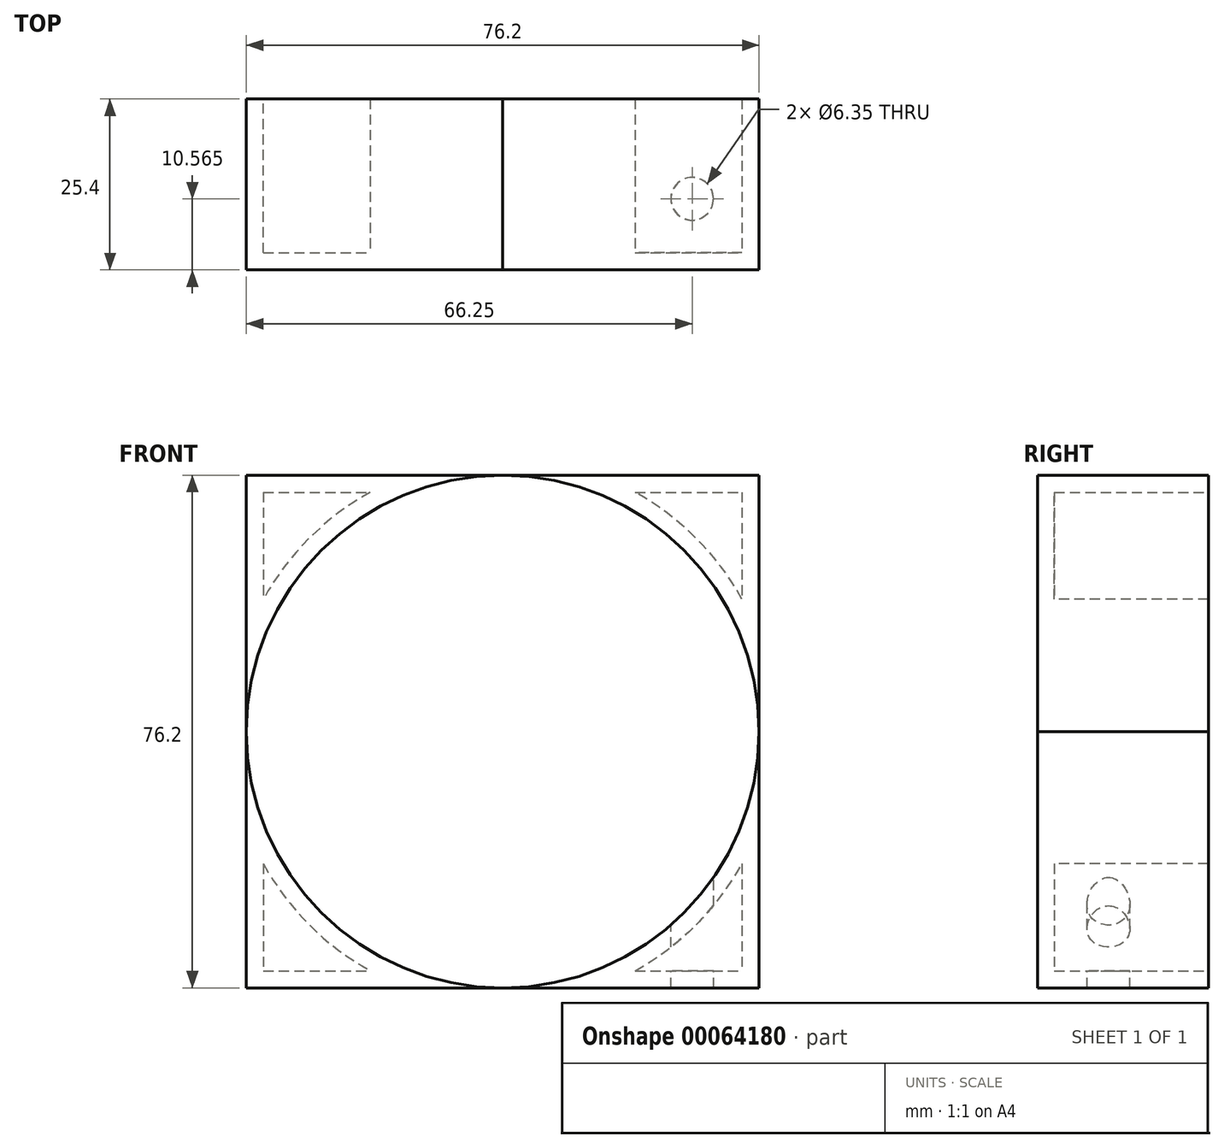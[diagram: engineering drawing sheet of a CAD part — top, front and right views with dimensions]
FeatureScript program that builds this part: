
annotation { "Feature Type Name" : "Feature", "Feature Type Description" : "" }
export const myFeature = defineFeature(function(context is Context, id is Id, definition is map)
    precondition{}
    {
        {
            var Q0;
            Q0=qCreatedBy(makeId("Front.planeOp"),FACE);
            var sketch = newSketch(context, id + "F0", { "sketchPlane" : qUnion([Q0])});
            skLineSegment(sketch, "E0.bottom", {"start": v(-38.1, 38.1) * mm, "end": v(38.1, 38.1) * mm});
            skLineSegment(sketch, "E0.top", {"start": v(-38.1, -38.1) * mm, "end": v(38.1, -38.1) * mm});
            skLineSegment(sketch, "E0.left", {"start": v(-38.1, 38.1) * mm, "end": v(-38.1, -38.1) * mm});
            skLineSegment(sketch, "E0.right", {"start": v(38.1, 38.1) * mm, "end": v(38.1, -38.1) * mm});
            skSolve(sketch);
        }
        {
            var Q0;
            Q0 = qSketchRegion(id + "F0", true);
            extrude(context, id + "F1", {"entities" : qUnion([Q0]), "depth" : 25.4 * mm});
        }
        {
            var Q0;
            Q0=makeQuery(id+"F1.opExtrude","CAP_FACE",FACE,{"disambiguationData":[OSD([sQuery(id+"F0.wireOp",EDGE,"E0.bottom"),sQuery(id+"F0.wireOp",EDGE,"E0.top"),sQuery(id+"F0.wireOp",EDGE,"E0.left"),sQuery(id+"F0.wireOp",EDGE,"E0.right")])],"isStart":false});
            var sketch = newSketch(context, id + "F2", { "sketchPlane" : qUnion([Q0])});
            skCircle(sketch, "E1", {"center": v(0, 0) * mm, "radius": 38.1 * mm});
            skSolve(sketch);
        }
        {
            var Q0;
            {var subQ0=sQuery(id+"F2.wireOp",EDGE,"E1");var subQ1=makeQuery(id+"F2.imprint","INTERSECT",VERTEX,{"derivedFrom":[makeQuery(id+"F1.opExtrude","CAP_EDGE",EDGE,{"disambiguationData":[OSD([sQuery(id+"F0.wireOp",EDGE,"E0.bottom")])],"isStart":false}),subQ0]});Q0=makeQuery(id+"F2.imprint","IMPRINT",FACE,{"disambiguationData":[TD([[makeQuery(id+"F2.imprint","IMPRINT",EDGE,{"disambiguationData":[TD([[subQ1,1.0]])],"derivedFrom":subQ0}),1.0]])]});}
            extrude(context, id + "F3", {"entities" : qUnion([Q0]), "operationType" : NewBodyOperationType.REMOVE, "oppositeDirection" : true, "depth" : 25.4 * mm});
        }
        {
            var Q0;
            {var subQ0=sQuery(id+"F0.wireOp",EDGE,"E0.bottom");var subQ1=sQuery(id+"F0.wireOp",EDGE,"E0.right");Q0=makeQuery(id+"F3.boolean.opBoolean","SPLIT",FACE,{"disambiguationData":[TD([makeQuery(id+"F1.opExtrude","SWEPT_FACE",FACE,{"disambiguationData":[OSD([subQ0])]}),makeQuery(id+"F1.opExtrude","SWEPT_FACE",FACE,{"disambiguationData":[OSD([subQ1])]}),makeQuery(id+"F3.opExtrude","SWEPT_FACE",FACE,{"disambiguationData":[OSD([sQuery(id+"F2.wireOp",EDGE,"E1")])]})])],"derivedFrom":makeQuery(id+"F1.opExtrude","CAP_FACE",FACE,{"disambiguationData":[OSD([subQ0,sQuery(id+"F0.wireOp",EDGE,"E0.top"),sQuery(id+"F0.wireOp",EDGE,"E0.left"),subQ1])],"isStart":true})});}
            var Q1;
            {var subQ0=sQuery(id+"F0.wireOp",EDGE,"E0.bottom");var subQ1=sQuery(id+"F0.wireOp",EDGE,"E0.left");Q1=makeQuery(id+"F3.boolean.opBoolean","SPLIT",FACE,{"disambiguationData":[TD([makeQuery(id+"F1.opExtrude","SWEPT_FACE",FACE,{"disambiguationData":[OSD([subQ0])]}),makeQuery(id+"F1.opExtrude","SWEPT_FACE",FACE,{"disambiguationData":[OSD([subQ1])]}),makeQuery(id+"F3.opExtrude","SWEPT_FACE",FACE,{"disambiguationData":[OSD([sQuery(id+"F2.wireOp",EDGE,"E1")])]})])],"derivedFrom":makeQuery(id+"F1.opExtrude","CAP_FACE",FACE,{"disambiguationData":[OSD([subQ0,sQuery(id+"F0.wireOp",EDGE,"E0.top"),subQ1,sQuery(id+"F0.wireOp",EDGE,"E0.right")])],"isStart":true})});}
            var Q2;
            {var subQ0=sQuery(id+"F0.wireOp",EDGE,"E0.top");var subQ1=sQuery(id+"F0.wireOp",EDGE,"E0.left");Q2=makeQuery(id+"F3.boolean.opBoolean","SPLIT",FACE,{"disambiguationData":[TD([makeQuery(id+"F1.opExtrude","SWEPT_FACE",FACE,{"disambiguationData":[OSD([subQ0])]}),makeQuery(id+"F1.opExtrude","SWEPT_FACE",FACE,{"disambiguationData":[OSD([subQ1])]}),makeQuery(id+"F3.opExtrude","SWEPT_FACE",FACE,{"disambiguationData":[OSD([sQuery(id+"F2.wireOp",EDGE,"E1")])]})])],"derivedFrom":makeQuery(id+"F1.opExtrude","CAP_FACE",FACE,{"disambiguationData":[OSD([sQuery(id+"F0.wireOp",EDGE,"E0.bottom"),subQ0,subQ1,sQuery(id+"F0.wireOp",EDGE,"E0.right")])],"isStart":true})});}
            var Q3;
            {var subQ0=sQuery(id+"F0.wireOp",EDGE,"E0.top");var subQ1=sQuery(id+"F0.wireOp",EDGE,"E0.right");Q3=makeQuery(id+"F3.boolean.opBoolean","SPLIT",FACE,{"disambiguationData":[TD([makeQuery(id+"F1.opExtrude","SWEPT_FACE",FACE,{"disambiguationData":[OSD([subQ0])]}),makeQuery(id+"F1.opExtrude","SWEPT_FACE",FACE,{"disambiguationData":[OSD([subQ1])]}),makeQuery(id+"F3.opExtrude","SWEPT_FACE",FACE,{"disambiguationData":[OSD([sQuery(id+"F2.wireOp",EDGE,"E1")])]})])],"derivedFrom":makeQuery(id+"F1.opExtrude","CAP_FACE",FACE,{"disambiguationData":[OSD([sQuery(id+"F0.wireOp",EDGE,"E0.bottom"),subQ0,sQuery(id+"F0.wireOp",EDGE,"E0.left"),subQ1])],"isStart":true})});}
            shell(context, id + "F4", {"entities" : qUnion([Q0, Q1, Q2, Q3]), "thickness" : 2.54 * mm});
        }
        {
            var Q0;
            {var subQ0=sQuery(id+"F0.wireOp",EDGE,"E0.right");var subQ3=sQuery(id+"F0.wireOp",EDGE,"E0.bottom");Q0=makeQuery(id+"F3.boolean.opBoolean","SPLIT",FACE,{"disambiguationData":[TD([makeQuery(id+"F1.opExtrude","SWEPT_FACE",FACE,{"disambiguationData":[OSD([subQ0])]})])],"derivedFrom":makeQuery(id+"F1.opExtrude","SWEPT_FACE",FACE,{"disambiguationData":[OSD([subQ3])]})});}
            var sketch = newSketch(context, id + "F5", { "sketchPlane" : qUnion([Q0])});
            skPoint(sketch, "E2", {"position": v(28.15, -14.84) * mm});
            skSolve(sketch);
        }
        {
            var Q0;
            Q0=sQuery(id+"F5.wireOp",VERTEX,"E2");
            var Q1;
            Q1=makeQuery(id+"F3.boolean.opBoolean","SPLIT",BODY,{"disambiguationData":[OD(1.0)],"derivedFrom":makeQuery(id+"F1.opExtrude","SWEPT_BODY",BODY,{"disambiguationData":[OSD([sQuery(id+"F0.wireOp",EDGE,"E0.bottom"),sQuery(id+"F0.wireOp",EDGE,"E0.top"),sQuery(id+"F0.wireOp",EDGE,"E0.left"),sQuery(id+"F0.wireOp",EDGE,"E0.right")])]})});
            var Q2;
            Q2=makeQuery(id+"F3.boolean.opBoolean","SPLIT",BODY,{"disambiguationData":[OD(3.0)],"derivedFrom":makeQuery(id+"F1.opExtrude","SWEPT_BODY",BODY,{"disambiguationData":[OSD([sQuery(id+"F0.wireOp",EDGE,"E0.bottom"),sQuery(id+"F0.wireOp",EDGE,"E0.top"),sQuery(id+"F0.wireOp",EDGE,"E0.left"),sQuery(id+"F0.wireOp",EDGE,"E0.right")])]})});
            hole(context, id + "F6", {"style" : HoleStyle.SIMPLE, "endStyle" : HoleEndStyle.THROUGH, "holeDiameter" : 6.35 * mm, "locations" : qUnion([Q0]), "scope" : qUnion([Q1, Q2]), "isTappedThrough" : true});
        }
    });
